# Revit family: Crealco Skyline Heavy Duty Sash Side Hung D
name_source: partatom
category: Windows
revit_build: Autodesk Revit 2014 (Build: 20130308_1515(x64)
units: mm (PartAtom-declared; Revit-internal decimal feet)

## types (6) — shared parameters
Corrected Mullion Configuration = 2 mm  [stored 0.00656168 ft]
Custom Sash Height = 1102 mm
Custom Window Width = 590 mm  [stored 1.9357 ft]
Description = Side Hung Type D Standard Sash Window
Frame Profile Thickness = 41 mm  [stored 0.134514 ft]
Heavy Duty Sash = Yes
Intruderprufe Insulated U Value = 2.84
Limit Fixed Pane Height Max = 3000 mm  [stored 9.84252 ft]
Limit Fixed Pane Height Min = 200 mm  [stored 0.656168 ft]
Limit Fixed Pane Width Max = 3000 mm  [stored 9.84252 ft]
Limit Fixed Pane Width Min = 200 mm  [stored 0.656168 ft]
Limit Sash Height Max = 1500 mm  [stored 4.92126 ft]
Limit Sash Height Min = 300 mm  [stored 0.984252 ft]
Limit Sash Width Max = 700 mm  [stored 2.29659 ft]
Limit Sash Width Min = 300 mm  [stored 0.984252 ft]
Limit Window Width Min = 388 mm
Manufacturer = Crealco
Max System DG Unit Thickness = 25 mm  [stored 0.082021 ft]
Model = Skyline
Rough Width = 3 mm  [stored 0.00984252 ft]
Sash Side Gap = 44 mm
Standard Mullion Different = No
Standard Sash = No
URL = www.crealco.co.za
Wall Closure = By host
zero-valued in all types: Custom Frame Offset From Exterior

## per-type parameters (varying)
| type | Clearvue Insulated LowE SHGC Value | Clearvue Insulated LowE U Value | Clearvue Insulated SHGC Value | Clearvue Insulated U Value | Clearvue SHGC Value | Clearvue U Value | Custom Windload | Custom Window Height | Energy Advantage SHGC Value | Energy Advantage U Value | Intruderprufe Insulated LowE SHGC Value | Intruderprufe Insulated LowE U Value | Intruderprufe Insulated SHGC Value | Intruderprufe LowE SHGC Value | Intruderprufe LowE U Value | Intruderprufe SHGC Value | Intruderprufe U Value | Toughened Safety SHGC Value | Toughened Safety U Value |
| 0600 x 1500mm 1000Pa | 0.782 | 4.13 | 0.782 | 4.18 | 0.487 | 6.15 | 1000 mm  [stored 3.28084 ft] | 1490 mm  [stored 4.88845 ft] | 0.439 | 5.18 | 0.649 | 2.81 | 0.649 | 0.409 | 5.05 | 0.459 | 6.03 | 0.487 | 6.15 |
| 0600 x 1500mm 1500Pa | 0.782 | 4.13 | 0.782 | 4.18 | 0.487 | 6.15 | 1500 mm  [stored 4.92126 ft] | 1490 mm  [stored 4.88845 ft] | 0.439 | 5.18 | 0.649 | 2.81 | 0.649 | 0.409 | 5.05 | 0.459 | 6.03 | 0.487 | 6.15 |
| 0600 x 1500mm 2000Pa | 0.782 | 4.13 | 0.782 | 4.18 | 0.487 | 6.15 | 2000 mm  [stored 6.56168 ft] | 1490 mm  [stored 4.88845 ft] | 0.439 | 5.18 | 0.649 | 2.81 | 0.649 | 0.409 | 5.05 | 0.459 | 6.03 | 0.487 | 6.15 |
| 0600 x 1800mm 1000Pa | 0.793 | 4.21 | 0.793 | 4.25 | 0.521 | 6.13 | 1000 mm  [stored 3.28084 ft] | 1790 mm  [stored 5.8727 ft] | 0.469 | 5.04 | 0.658 | 2.82 | 0.658 | 0.437 | 4.9 | 0.491 | 5.98 | 0.521 | 6.13 |
| 0600 x 1800mm 1500Pa | 0.793 | 4.21 | 0.793 | 4.25 | 0.521 | 6.13 | 1500 mm  [stored 4.92126 ft] | 1790 mm  [stored 5.8727 ft] | 0.469 | 5.04 | 0.658 | 2.82 | 0.658 | 0.437 | 4.9 | 0.491 | 5.98 | 0.521 | 6.13 |
| 0600 x 1800mm 2000Pa | 0.793 | 4.21 | 0.793 | 4.25 | 0.521 | 6.13 | 2000 mm  [stored 6.56168 ft] | 1790 mm  [stored 5.8727 ft] | 0.469 | 5.04 | 0.658 | 2.82 | 0.658 | 0.437 | 4.9 | 0.491 | 5.98 | 0.521 | 6.13 |

note: [stored X ft] marks values corroborated as IEEE doubles in the binary element streams (Revit-internal decimal feet)

## geometry (parser evidence)
native form markers: Sweep x18
no freeform markers — native parametric forms only
